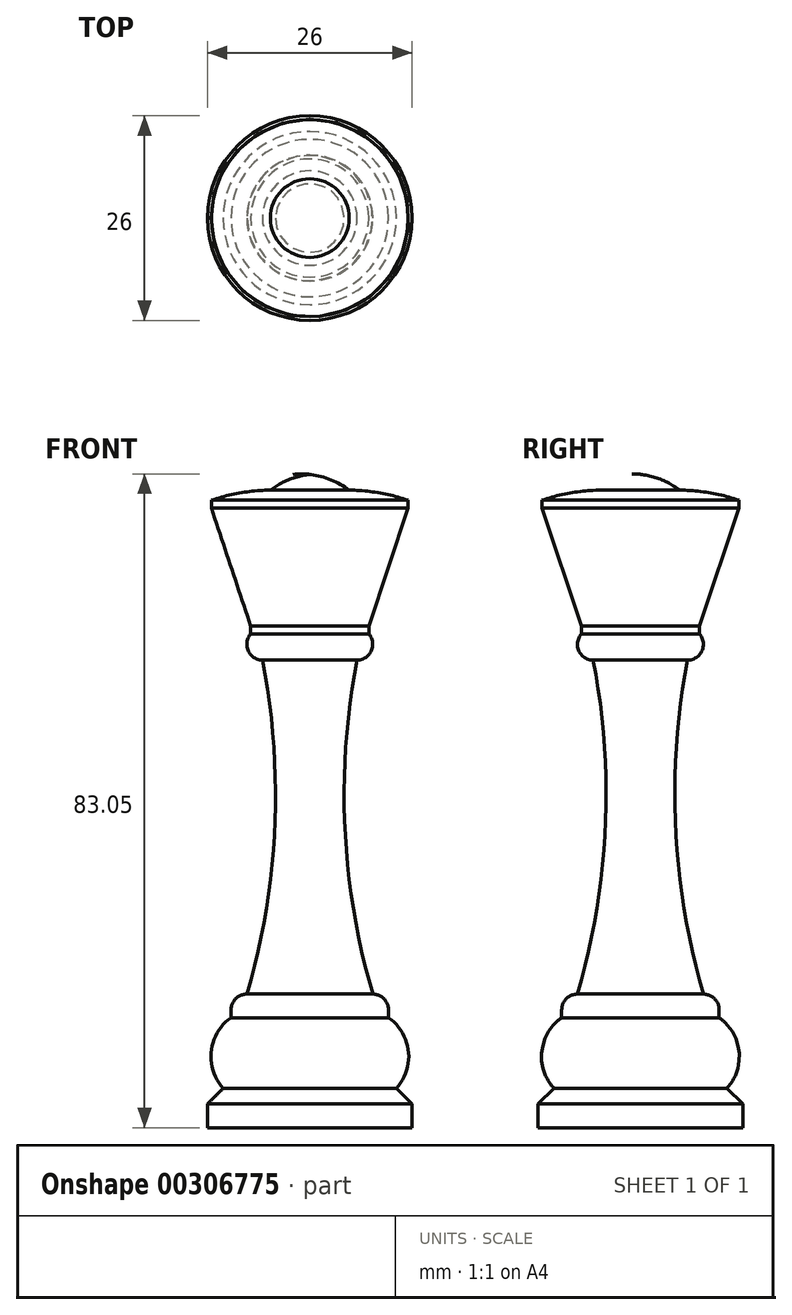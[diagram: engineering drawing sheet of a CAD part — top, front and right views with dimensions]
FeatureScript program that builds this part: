
annotation { "Feature Type Name" : "Feature", "Feature Type Description" : "" }
export const myFeature = defineFeature(function(context is Context, id is Id, definition is map)
    precondition{}
    {
        {
            var Q0;
            Q0=qCreatedBy(makeId("Front.planeOp"),FACE);
            var sketch = newSketch(context, id + "F0", { "sketchPlane" : qUnion([Q0])});
            skArc(sketch, "E0", {"start": v(5, -2) * mm, "mid": v(2.64, -0.66) * mm, "end": v(0, 0) * mm});
            skArc(sketch, "E1", {"start": v(12.5, -3.27) * mm, "mid": v(8.8, -2.35) * mm, "end": v(5, -2) * mm});
            skLineSegment(sketch, "E2", {"start": v(12.5, -3.27) * mm, "end": v(12.5, -4.27) * mm});
            skLineSegment(sketch, "E3", {"start": v(12.5, -4.27) * mm, "end": v(7.5, -19.27) * mm});
            skLineSegment(sketch, "E4", {"start": v(7.5, -19.27) * mm, "end": v(7.5, -20.27) * mm});
            skArc(sketch, "E5", {"start": v(6, -23.59) * mm, "mid": v(7.82, -22.41) * mm, "end": v(7.5, -20.27) * mm});
            skArc(sketch, "E6", {"start": v(6, -23.6) * mm, "mid": v(4.46, -44.92) * mm, "end": v(8, -66.02) * mm});
            skArc(sketch, "E7", {"start": v(10, -68.02) * mm, "mid": v(9.41, -66.6) * mm, "end": v(8, -66.02) * mm});
            skLineSegment(sketch, "E8", {"start": v(10, -68.02) * mm, "end": v(10, -69.02) * mm});
            skLineSegment(sketch, "E9", {"start": v(13, -80) * mm, "end": v(13, -83) * mm});
            skLineSegment(sketch, "E10", {"start": v(13, -83) * mm, "end": v(0, -83) * mm});
            skLineSegment(sketch, "E11", {"start": v(0, -83) * mm, "end": v(0, 0) * mm});
            skArc(sketch, "E12", {"start": v(11, -78) * mm, "mid": v(12.53, -73.28) * mm, "end": v(10, -69.02) * mm});
            skLineSegment(sketch, "E13", {"start": v(11, -78) * mm, "end": v(13, -80) * mm});
            skSolve(sketch);
        }
        {
            var Q0;
            Q0=makeQuery(id+"F0.imprint","IMPRINT",FACE,{"disambiguationData":[TD([[makeQuery(id+"F0.imprint","IMPRINT",EDGE,{"derivedFrom":sQuery(id+"F0.wireOp",EDGE,"E0")}),1.0]])]});
            var Q1;
            Q1=sQuery(id+"F0.wireOp",EDGE,"E11");
            revolve(context, id + "F1", {"entities" : qUnion([Q0]), "axis" : qUnion([Q1]), "revolveType" : RevolveType.FULL});
        }
    });
